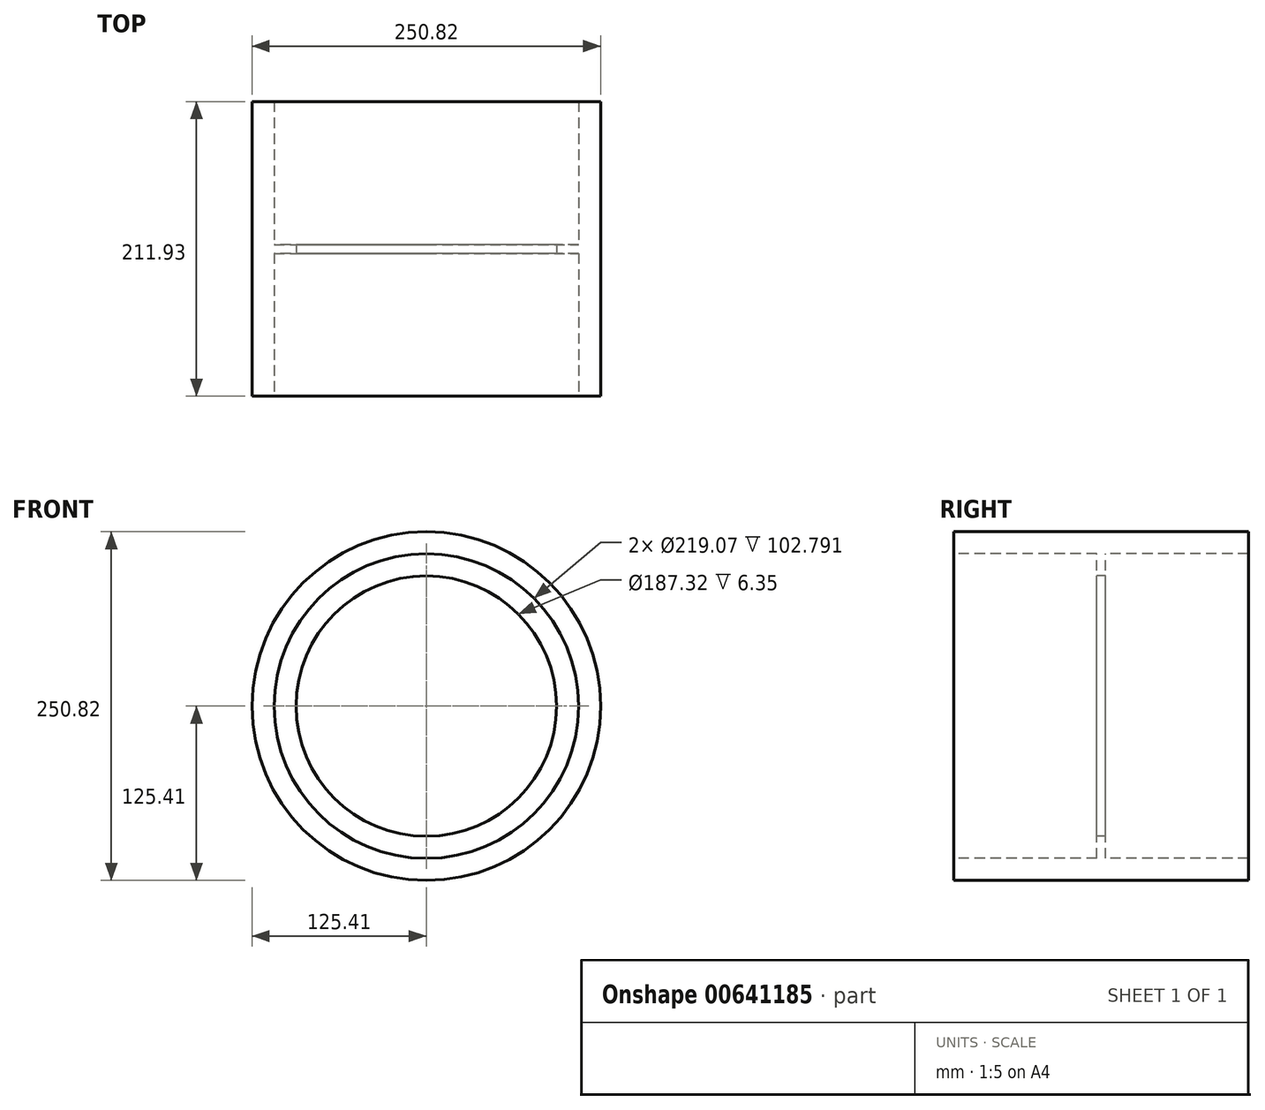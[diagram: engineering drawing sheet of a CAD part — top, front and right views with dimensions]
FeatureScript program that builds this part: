
annotation { "Feature Type Name" : "Feature", "Feature Type Description" : "" }
export const myFeature = defineFeature(function(context is Context, id is Id, definition is map)
    precondition{}
    {
        {
            var Q0;
            Q0=qCreatedBy(makeId("Right.planeOp"),FACE);
            var sketch = newSketch(context, id + "F0", { "sketchPlane" : qUnion([Q0])});
            skLineSegment(sketch, "E0", {"start": v(-122.47, 125.41) * mm, "end": v(89.46, 125.41) * mm});
            skLineSegment(sketch, "E1", {"start": v(-122.47, 125.41) * mm, "end": v(-122.47, 109.54) * mm});
            skLineSegment(sketch, "E2", {"start": v(-122.47, 109.54) * mm, "end": v(-19.68, 109.54) * mm});
            skLineSegment(sketch, "E3", {"start": v(-19.68, 109.54) * mm, "end": v(-19.68, 93.66) * mm});
            skLineSegment(sketch, "E4", {"start": v(-19.68, 93.66) * mm, "end": v(-13.33, 93.66) * mm});
            skLineSegment(sketch, "E5", {"start": v(-13.33, 93.66) * mm, "end": v(-13.33, 109.54) * mm});
            skLineSegment(sketch, "E6", {"start": v(89.46, 109.54) * mm, "end": v(89.46, 125.41) * mm});
            skLineSegment(sketch, "E7", {"start": v(-13.33, 109.54) * mm, "end": v(89.46, 109.54) * mm});
            skLineSegment(sketch, "E8", {"start": v(-122.47, 109.54) * mm, "end": v(-122.47, 0) * mm});
            skLineSegment(sketch, "E9", {"start": v(-122.47, 0) * mm, "end": v(89.46, 0) * mm});
            skLineSegment(sketch, "E10", {"start": v(89.46, 0) * mm, "end": v(89.46, 109.54) * mm});
            skSolve(sketch);
        }
        {
            var Q0;
            Q0=makeQuery(id+"F0.imprint","IMPRINT",FACE,{"disambiguationData":[TD([[makeQuery(id+"F0.imprint","IMPRINT",EDGE,{"derivedFrom":sQuery(id+"F0.wireOp",EDGE,"E0")}),-1.0]])]});
            var Q1;
            Q1=sQuery(id+"F0.wireOp",EDGE,"E9");
            revolve(context, id + "F1", {"entities" : qUnion([Q0]), "axis" : qUnion([Q1]), "revolveType" : RevolveType.FULL});
        }
        {
            var Q0;
            Q0=makeQuery(id+"F1.opRevolve","SWEPT_FACE",FACE,{"disambiguationData":[OSD([sQuery(id+"F0.wireOp",EDGE,"E3")])]});
            var sketch = newSketch(context, id + "F2", { "sketchPlane" : qUnion([Q0])});
            skCircle(sketch, "E11", {"center": v(0, 0) * mm, "radius": 33.22 * mm, "construction": true});
            skSolve(sketch);
        }
        {
            var Q0;
            Q0=makeQuery(id+"F1.opRevolve","SWEPT_FACE",FACE,{"disambiguationData":[OSD([sQuery(id+"F0.wireOp",EDGE,"E5")])]});
            var sketch = newSketch(context, id + "F3", { "sketchPlane" : qUnion([Q0])});
            skCircle(sketch, "E12", {"center": v(0, 0) * mm, "radius": 38.49 * mm, "construction": true});
            skSolve(sketch);
        }
    });
